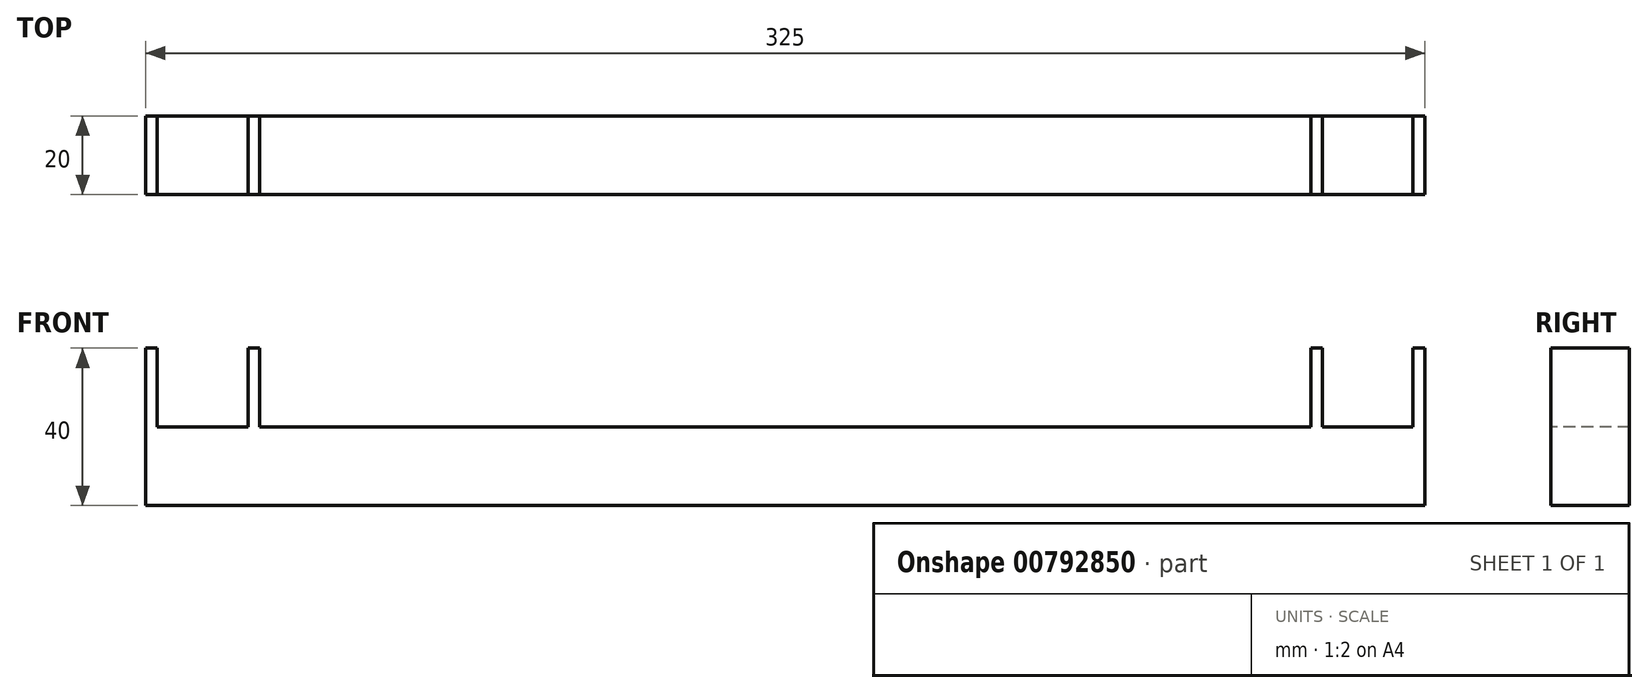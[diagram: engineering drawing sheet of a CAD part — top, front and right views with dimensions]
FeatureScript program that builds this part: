
annotation { "Feature Type Name" : "Feature", "Feature Type Description" : "" }
export const myFeature = defineFeature(function(context is Context, id is Id, definition is map)
    precondition{}
    {
        {
            var Q0;
            Q0=qCreatedBy(makeId("Front.planeOp"),FACE);
            var sketch = newSketch(context, id + "F0", { "sketchPlane" : qUnion([Q0])});
            skLineSegment(sketch, "E0.bottom", {"start": v(-162.5, -10) * mm, "end": v(162.5, -10) * mm});
            skLineSegment(sketch, "E0.top", {"start": v(-162.5, 10) * mm, "end": v(162.5, 10) * mm});
            skLineSegment(sketch, "E0.left", {"start": v(-162.5, -10) * mm, "end": v(-162.5, 10) * mm});
            skLineSegment(sketch, "E0.right", {"start": v(162.5, -10) * mm, "end": v(162.5, 10) * mm});
            skPoint(sketch, "E0.middle", {"position": v(0, 0) * mm});
            skSolve(sketch);
        }
        {
            var Q0;
            Q0 = qSketchRegion(id + "F0", true);
            extrude(context, id + "F1", {"entities" : qUnion([Q0]), "depth" : 20 * mm, "offsetDistance" : 25 * mm});
        }
        {
            var Q0;
            Q0=makeQuery(id+"F1.opExtrude","SWEPT_FACE",FACE,{"disambiguationData":[OSD([sQuery(id+"F0.wireOp",EDGE,"E0.top")])]});
            var sketch = newSketch(context, id + "F2", { "sketchPlane" : qUnion([Q0])});
            skLineSegment(sketch, "E1.bottom", {"start": v(162.5, 0) * mm, "end": v(159.5, 0) * mm});
            skLineSegment(sketch, "E1.top", {"start": v(162.5, -20) * mm, "end": v(159.5, -20) * mm});
            skLineSegment(sketch, "E1.left", {"start": v(162.5, 0) * mm, "end": v(162.5, -20) * mm});
            skLineSegment(sketch, "E1.right", {"start": v(159.5, 0) * mm, "end": v(159.5, -20) * mm});
            skLineSegment(sketch, "E2.bottom", {"start": v(136.5, -20) * mm, "end": v(133.5, -20) * mm});
            skLineSegment(sketch, "E2.top", {"start": v(136.5, 0) * mm, "end": v(133.5, 0) * mm});
            skLineSegment(sketch, "E2.left", {"start": v(136.5, -20) * mm, "end": v(136.5, 0) * mm});
            skLineSegment(sketch, "E2.right", {"start": v(133.5, -20) * mm, "end": v(133.5, 0) * mm});
            skLineSegment(sketch, "E3.bottom", {"start": v(-162.5, 0) * mm, "end": v(-159.5, 0) * mm});
            skLineSegment(sketch, "E3.top", {"start": v(-162.5, -20) * mm, "end": v(-159.5, -20) * mm});
            skLineSegment(sketch, "E3.left", {"start": v(-162.5, 0) * mm, "end": v(-162.5, -20) * mm});
            skLineSegment(sketch, "E3.right", {"start": v(-159.5, 0) * mm, "end": v(-159.5, -20) * mm});
            skLineSegment(sketch, "E4.bottom", {"start": v(-136.5, 0) * mm, "end": v(-133.5, 0) * mm});
            skLineSegment(sketch, "E4.top", {"start": v(-136.5, -20) * mm, "end": v(-133.5, -20) * mm});
            skLineSegment(sketch, "E4.left", {"start": v(-136.5, 0) * mm, "end": v(-136.5, -20) * mm});
            skLineSegment(sketch, "E4.right", {"start": v(-133.5, 0) * mm, "end": v(-133.5, -20) * mm});
            skSolve(sketch);
        }
        {
            var Q0;
            Q0 = qSketchRegion(id + "F2", true);
            extrude(context, id + "F3", {"entities" : qUnion([Q0]), "operationType" : NewBodyOperationType.ADD, "depth" : 20 * mm, "offsetDistance" : 25 * mm});
        }
    });
